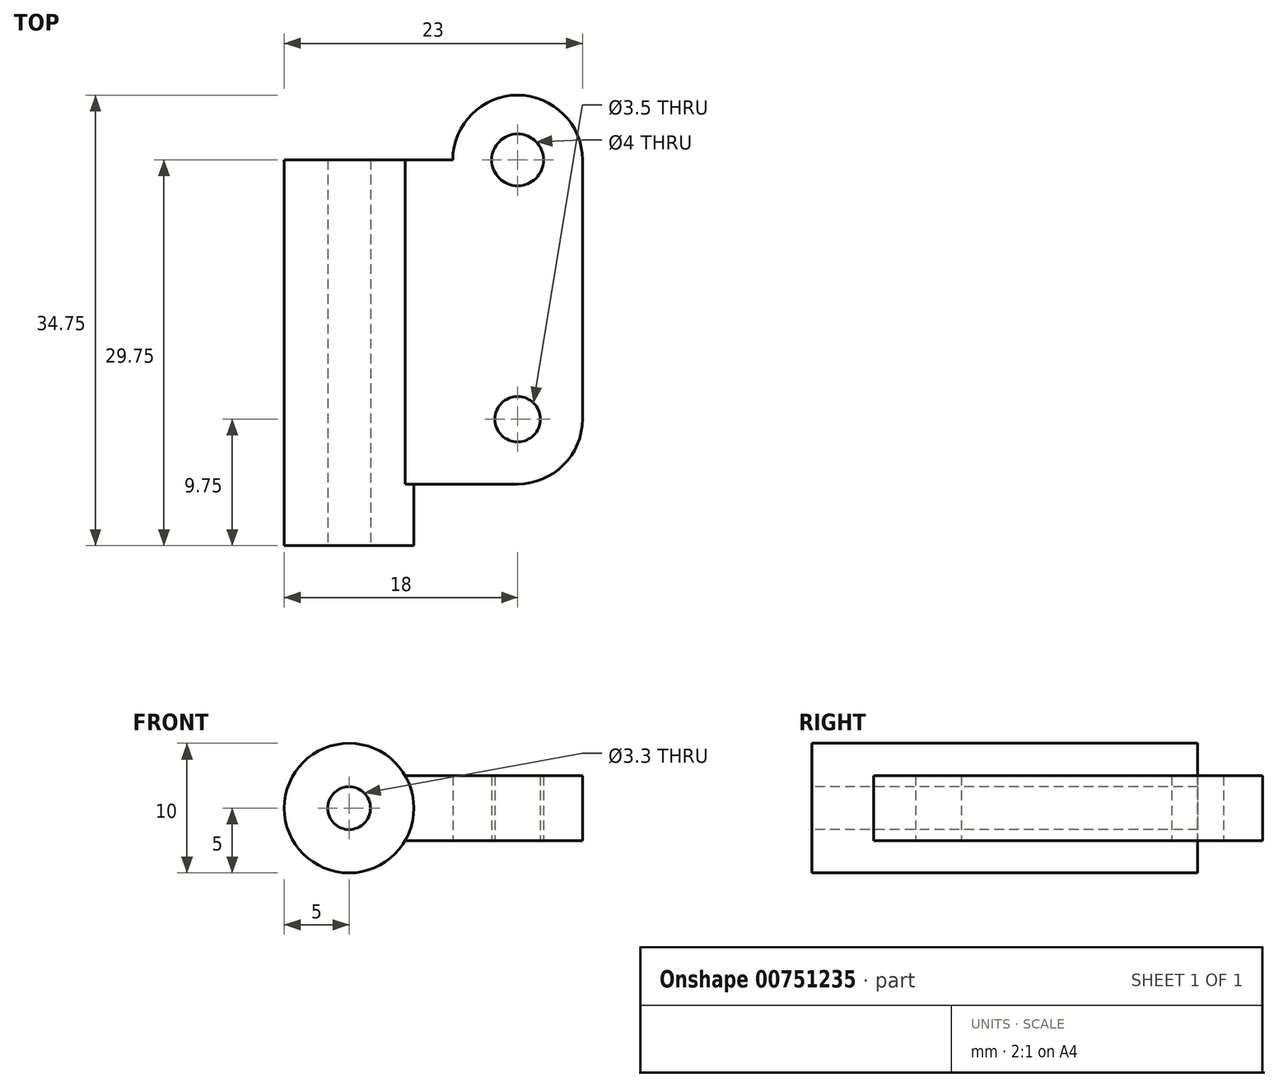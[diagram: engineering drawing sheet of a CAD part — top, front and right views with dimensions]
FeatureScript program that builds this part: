
annotation { "Feature Type Name" : "Feature", "Feature Type Description" : "" }
export const myFeature = defineFeature(function(context is Context, id is Id, definition is map)
    precondition{}
    {
        {
            var Q0;
            Q0=qCreatedBy(makeId("Top.planeOp"),FACE);
            var sketch = newSketch(context, id + "F0", { "sketchPlane" : qUnion([Q0])});
            skLineSegment(sketch, "E0", {"start": v(0, -10) * mm, "end": v(0, 10) * mm, "construction": true});
            skPoint(sketch, "E1", {"position": v(0, 0) * mm});
            skLineSegment(sketch, "E2", {"start": v(0, 10) * mm, "end": v(-13, 10) * mm, "construction": true});
            skLineSegment(sketch, "E3", {"start": v(-13, 10) * mm, "end": v(-13, -19.75) * mm, "construction": true});
            skLineSegment(sketch, "E4", {"start": v(-13, 10) * mm, "end": v(-13, -16.72) * mm, "construction": true});
            skLineSegment(sketch, "E5", {"start": v(-18, 10) * mm, "end": v(-8, 10) * mm});
            skPoint(sketch, "E6", {"position": v(-13, 10) * mm});
            skCircle(sketch, "E7", {"center": v(0, 10) * mm, "radius": 2 * mm});
            skCircle(sketch, "E8", {"center": v(0, -10) * mm, "radius": 1.75 * mm});
            skLineSegment(sketch, "E9", {"start": v(2, 10) * mm, "end": v(2, -10) * mm, "construction": true});
            skCircle(sketch, "E10", {"center": v(0, -10) * mm, "radius": 2 * mm, "construction": true});
            skLineSegment(sketch, "E11", {"start": v(-18, -19.75) * mm, "end": v(-8, -19.75) * mm});
            skPoint(sketch, "E12", {"position": v(-13, -19.75) * mm});
            skLineSegment(sketch, "E13", {"start": v(-18, 10) * mm, "end": v(-18, -19.75) * mm});
            skLineSegment(sketch, "E14", {"start": v(-8, 10) * mm, "end": v(-8, -19.75) * mm});
            skArc(sketch, "E15.0", {"start": v(2, 5.42) * mm, "mid": v(2.74, 14.18) * mm, "end": v(-5, 10) * mm});
            skArc(sketch, "E16.0", {"start": v(0, -15) * mm, "mid": v(3.54, -13.54) * mm, "end": v(5, -10) * mm});
            skLineSegment(sketch, "E17", {"start": v(5, -10) * mm, "end": v(5, 10) * mm});
            skLineSegment(sketch, "E18", {"start": v(-8, 10) * mm, "end": v(-5, 10) * mm});
            skLineSegment(sketch, "E19", {"start": v(0, -15) * mm, "end": v(-8, -15) * mm});
            skSolve(sketch);
        }
        {
            var Q0;
            Q0=makeQuery(id+"F0.imprint","IMPRINT",FACE,{"disambiguationData":[TD([[makeQuery(id+"F0.imprint","IMPRINT",EDGE,{"derivedFrom":sQuery(id+"F0.wireOp",EDGE,"E7")}),-1.0]])]});
            extrude(context, id + "F1", {"entities" : qUnion([Q0]), "depth" : 5 * mm, "offsetDistance" : 25 * mm});
        }
        {
            var Q0;
            {var subQ2=sQuery(id+"F0.wireOp",EDGE,"E5");Q0=makeQuery(id+"F0.imprint","IMPRINT",FACE,{"disambiguationData":[TD([[makeQuery(id+"F0.imprint","IMPRINT",EDGE,{"derivedFrom":subQ2}),-1.0]])]});}
            extrude(context, id + "F2", {"entities" : qUnion([Q0]), "operationType" : NewBodyOperationType.ADD, "depth" : 7.5 * mm, "offsetDistance" : 25 * mm});
        }
        {
            var Q0;
            {var subQ2=sQuery(id+"F0.wireOp",EDGE,"E5");Q0=makeQuery(id+"F0.imprint","IMPRINT",FACE,{"disambiguationData":[TD([[makeQuery(id+"F0.imprint","IMPRINT",EDGE,{"derivedFrom":subQ2}),-1.0]])]});}
            extrude(context, id + "F3", {"entities" : qUnion([Q0]), "operationType" : NewBodyOperationType.ADD, "oppositeDirection" : true, "depth" : 2.5 * mm, "offsetDistance" : 25 * mm});
        }
        {
            var Q0;
            {var subQ0=sQuery(id+"F0.wireOp",EDGE,"E11");Q0=makeQuery(id+"F3.boolean.opBoolean","MERGE",FACE,{"derivedFrom":[makeQuery(id+"F2.opExtrude","SWEPT_FACE",FACE,{"disambiguationData":[OSD([subQ0])]}),makeQuery(id+"F3.opExtrude","SWEPT_FACE",FACE,{"disambiguationData":[OSD([subQ0])]})]});}
            var sketch = newSketch(context, id + "F4", { "sketchPlane" : qUnion([Q0])});
            skCircle(sketch, "E20", {"center": v(-13, 2.5) * mm, "radius": 1.65 * mm});
            skPoint(sketch, "E20.centerSnap0", {"position": v(-18, 2.5) * mm});
            skPoint(sketch, "E20.centerSnap1", {"position": v(-13, -2.5) * mm});
            skSolve(sketch);
        }
        {
            var Q0;
            Q0=makeQuery(id+"F4.imprint","IMPRINT",FACE,{"disambiguationData":[TD([[makeQuery(id+"F4.imprint","IMPRINT",EDGE,{"derivedFrom":sQuery(id+"F4.wireOp",EDGE,"E20")}),1.0]])]});
            var Q1;
            {var subQ0=sQuery(id+"F0.wireOp",EDGE,"E5");Q1=makeQuery(id+"F3.boolean.opBoolean","MERGE",FACE,{"derivedFrom":[makeQuery(id+"F2.opExtrude","SWEPT_FACE",FACE,{"disambiguationData":[OSD([subQ0])]}),makeQuery(id+"F3.opExtrude","SWEPT_FACE",FACE,{"disambiguationData":[OSD([subQ0])]})]});}
            extrude(context, id + "F5", {"entities" : qUnion([Q0]), "operationType" : NewBodyOperationType.REMOVE, "endBound" : BoundingType.UP_TO_SURFACE, "oppositeDirection" : true, "depth" : 40 * mm, "endBoundEntityFace" : qUnion([Q1]), "offsetDistance" : 25 * mm});
        }
        {
            var Q0;
            Q0=makeQuery(id+"F2.opExtrude","CAP_EDGE",EDGE,{"disambiguationData":[OSD([sQuery(id+"F0.wireOp",EDGE,"E13")])],"isStart":false});
            var Q1;
            Q1=makeQuery(id+"F3.opExtrude","CAP_EDGE",EDGE,{"disambiguationData":[OSD([sQuery(id+"F0.wireOp",EDGE,"E13")])],"isStart":false});
            var Q2;
            Q2=makeQuery(id+"F2.opExtrude","CAP_EDGE",EDGE,{"disambiguationData":[OSD([sQuery(id+"F0.wireOp",EDGE,"E14")])],"isStart":false});
            var Q3;
            Q3=makeQuery(id+"F3.opExtrude","CAP_EDGE",EDGE,{"disambiguationData":[OSD([sQuery(id+"F0.wireOp",EDGE,"E14")])],"isStart":false});
            fillet(context, id + "F6", {"entities" : qUnion([Q0, Q1, Q2, Q3]), "radius" : 5 * mm, "tangentPropagation" : true, "allowEdgeOverflow" : false});
        }
    });
